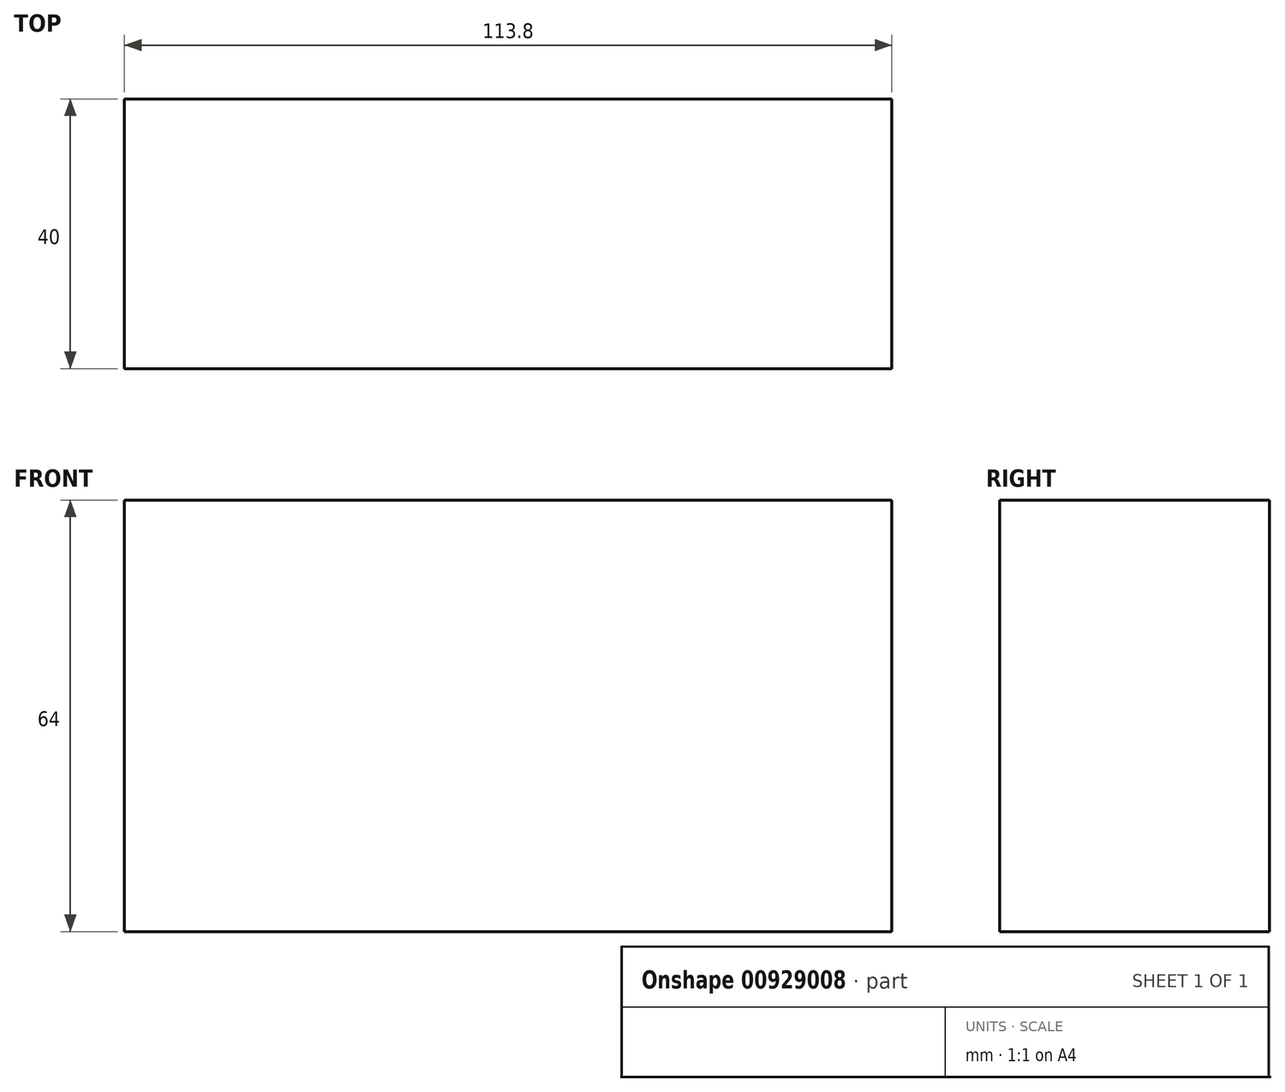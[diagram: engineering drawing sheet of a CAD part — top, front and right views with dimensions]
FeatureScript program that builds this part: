
annotation { "Feature Type Name" : "Feature", "Feature Type Description" : "" }
export const myFeature = defineFeature(function(context is Context, id is Id, definition is map)
    precondition{}
    {
        {
            var Q0;
            Q0=qCreatedBy(makeId("Front.planeOp"),FACE);
            var sketch = newSketch(context, id + "F0", { "sketchPlane" : qUnion([Q0])});
            skLineSegment(sketch, "E0.bottom", {"start": v(60, 34) * mm, "end": v(-60, 34) * mm});
            skLineSegment(sketch, "E0.top", {"start": v(60, -34) * mm, "end": v(-60, -34) * mm});
            skLineSegment(sketch, "E0.left", {"start": v(60, 34) * mm, "end": v(60, -34) * mm});
            skLineSegment(sketch, "E0.right", {"start": v(-60, 34) * mm, "end": v(-60, -34) * mm});
            skPoint(sketch, "E0.middle", {"position": v(0, 0) * mm});
            skLineSegment(sketch, "E1.bottom", {"start": v(56.9, 32) * mm, "end": v(-56.9, 32) * mm});
            skLineSegment(sketch, "E1.top", {"start": v(56.9, -32) * mm, "end": v(-56.9, -32) * mm});
            skLineSegment(sketch, "E1.left", {"start": v(56.9, 32) * mm, "end": v(56.9, -32) * mm});
            skLineSegment(sketch, "E1.right", {"start": v(-56.9, 32) * mm, "end": v(-56.9, -32) * mm});
            skSolve(sketch);
        }
        {
            var Q0;
            Q0=makeQuery(id+"F0.imprint","IMPRINT",FACE,{"disambiguationData":[TD([[makeQuery(id+"F0.imprint","IMPRINT",EDGE,{"derivedFrom":sQuery(id+"F0.wireOp",EDGE,"E1.bottom")}),1.0]])]});
            extrude(context, id + "F1", {"entities" : qUnion([Q0]), "oppositeDirection" : true, "depth" : 40 * mm, "offsetDistance" : 25 * mm});
        }
    });
